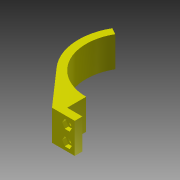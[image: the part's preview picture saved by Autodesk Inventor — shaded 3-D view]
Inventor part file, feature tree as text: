
AUTODESK INVENTOR PART (.ipt)
format: ipt  version: 2013 (Build 170138000, 138)  size: 124,928 bytes
history: native  units: mm
features: extrude x3, sketch x3
ambient origin geometry x8: Origin, YZ Plane, XZ Plane, XY Plane, X Axis, Y Axis, Z Axis, Center Point
bodies: Solid1 (feature_tree)
feature tree (6):
  extrude  "Extrusion1"  Depth=5.0mm
  extrude  "Extrusion2"  Depth=30.1625mm
  extrude  "Extrusion3"  Depth=12.5mm
  sketch  "Sketch1"  dims[d0=60.325mm d2=5.0mm]
  sketch  "Sketch2"  dims[d3=60.0deg d4=30.1625mm]
  sketch  "Sketch3"  dims[d5=35.1625mm d6=12.5mm d7=10.0mm d8=5.0mm d9=20.0mm d10=0.0mm d11=3.2mm d13=5.0mm d14=5.0mm d15=5.0mm d16=20.0mm d17=0.0mm d18=5.65mm d19=2.5mm d20=0.0mm]
